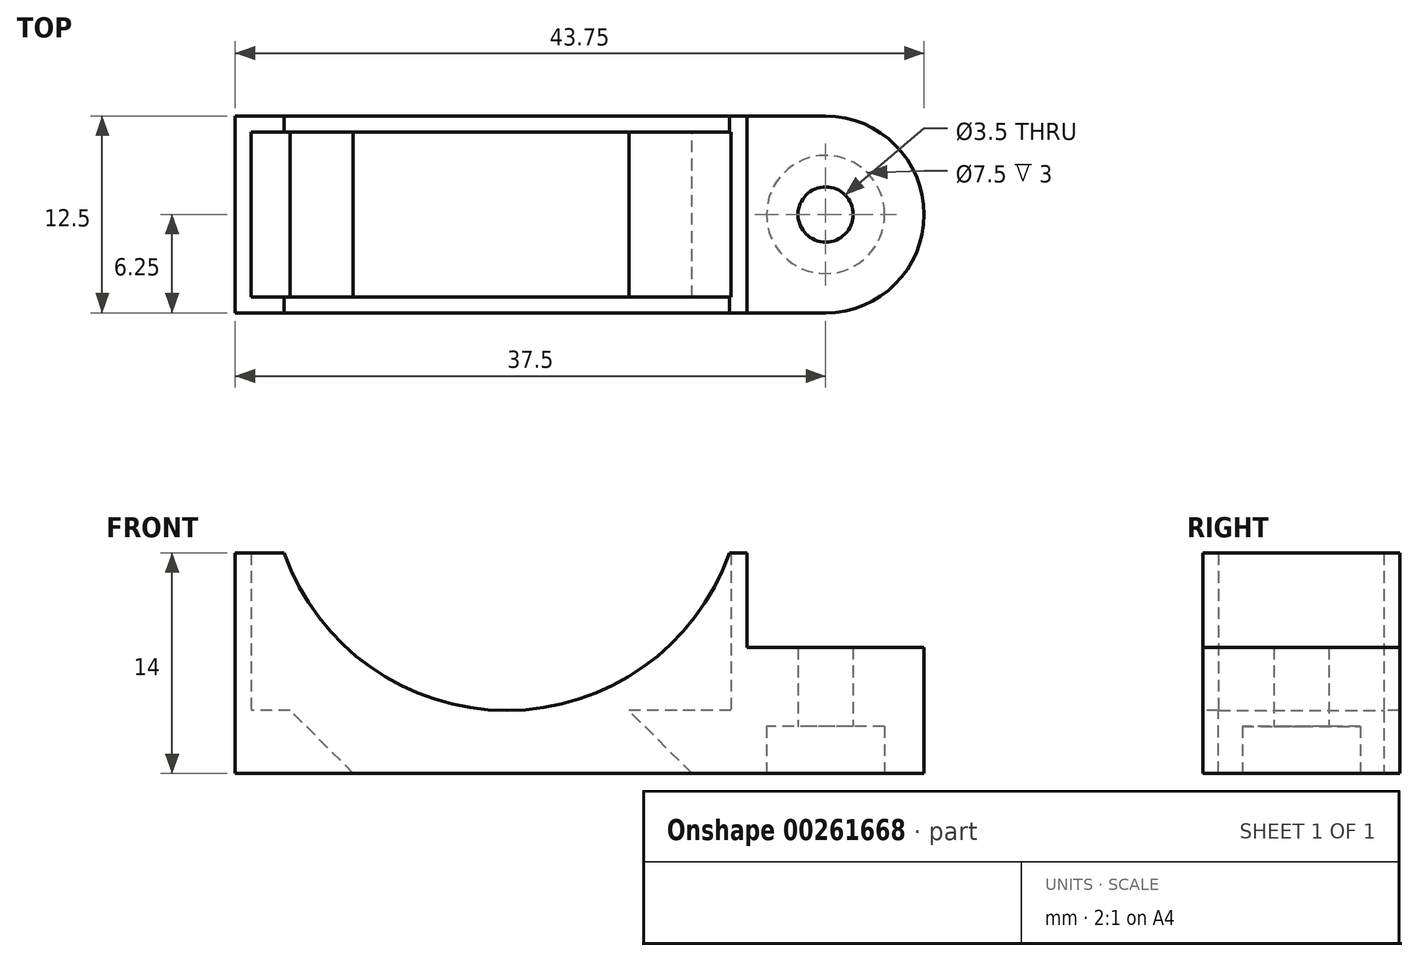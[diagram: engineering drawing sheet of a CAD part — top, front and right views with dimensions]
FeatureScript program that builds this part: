
annotation { "Feature Type Name" : "Feature", "Feature Type Description" : "" }
export const myFeature = defineFeature(function(context is Context, id is Id, definition is map)
    precondition{}
    {
        {
            var Q0;
            Q0=qCreatedBy(makeId("Top.planeOp"),FACE);
            var sketch = newSketch(context, id + "F0", { "sketchPlane" : qUnion([Q0])});
            skLineSegment(sketch, "E0.bottom", {"start": v(15.25, -5.25) * mm, "end": v(-15.25, -5.25) * mm});
            skLineSegment(sketch, "E0.top", {"start": v(15.25, 5.25) * mm, "end": v(-15.25, 5.25) * mm});
            skLineSegment(sketch, "E0.left", {"start": v(15.25, -5.25) * mm, "end": v(15.25, 5.25) * mm});
            skLineSegment(sketch, "E0.right", {"start": v(-15.25, -5.25) * mm, "end": v(-15.25, 5.25) * mm});
            skPoint(sketch, "E0.middle", {"position": v(0, 0) * mm});
            skLineSegment(sketch, "E1.0", {"start": v(-16.25, -6.25) * mm, "end": v(-16.25, 6.25) * mm});
            skLineSegment(sketch, "E1.1", {"start": v(16.25, -6.25) * mm, "end": v(-16.25, -6.25) * mm});
            skLineSegment(sketch, "E1.2", {"start": v(16.25, -6.25) * mm, "end": v(16.25, 6.25) * mm});
            skLineSegment(sketch, "E1.3", {"start": v(16.25, 6.25) * mm, "end": v(-16.25, 6.25) * mm});
            skArc(sketch, "E2", {"start": v(21.25, -6.25) * mm, "mid": v(27.5, 0) * mm, "end": v(21.25, 6.25) * mm});
            skLineSegment(sketch, "E3", {"start": v(16.25, -6.25) * mm, "end": v(21.25, -6.25) * mm});
            skLineSegment(sketch, "E4", {"start": v(16.25, 6.25) * mm, "end": v(21.25, 6.25) * mm});
            skLineSegment(sketch, "E5", {"start": v(8.75, 5.25) * mm, "end": v(8.75, -5.25) * mm});
            skCircle(sketch, "E6", {"center": v(21.25, 0) * mm, "radius": 1.75 * mm});
            skLineSegment(sketch, "E7", {"start": v(-8.75, -5.25) * mm, "end": v(-8.75, 5.25) * mm});
            skSolve(sketch);
        }
        {
            var Q0;
            Q0=makeQuery(id+"F0.imprint","IMPRINT",FACE,{"disambiguationData":[TD([[makeQuery(id+"F0.imprint","IMPRINT",EDGE,{"derivedFrom":sQuery(id+"F0.wireOp",EDGE,"E1.2")}),-1.0]])]});
            extrude(context, id + "F1", {"entities" : qUnion([Q0]), "depth" : 8 * mm});
        }
        {
            var Q0;
            {var subQ1=sQuery(id+"F0.wireOp",EDGE,"E0.left");Q0=makeQuery(id+"F0.imprint","IMPRINT",FACE,{"disambiguationData":[TD([[makeQuery(id+"F0.imprint","IMPRINT",EDGE,{"derivedFrom":subQ1}),-1.0]])]});}
            extrude(context, id + "F2", {"entities" : qUnion([Q0]), "operationType" : NewBodyOperationType.ADD, "depth" : 14 * mm});
        }
        {
            var Q0;
            {var subQ0=sQuery(id+"F0.wireOp",EDGE,"E0.left");Q0=makeQuery(id+"F0.imprint","IMPRINT",FACE,{"disambiguationData":[TD([[makeQuery(id+"F0.imprint","IMPRINT",EDGE,{"derivedFrom":subQ0}),1.0]])]});}
            var Q1;
            {var subQ0=sQuery(id+"F0.wireOp",EDGE,"E0.right");Q1=makeQuery(id+"F0.imprint","IMPRINT",FACE,{"disambiguationData":[TD([[makeQuery(id+"F0.imprint","IMPRINT",EDGE,{"derivedFrom":subQ0}),-1.0]])]});}
            extrude(context, id + "F3", {"entities" : qUnion([Q0, Q1]), "operationType" : NewBodyOperationType.ADD, "depth" : 4 * mm});
        }
        {
            var Q0;
            Q0=makeQuery(id+"F3.opExtrude","CAP_EDGE",EDGE,{"disambiguationData":[OSD([sQuery(id+"F0.wireOp",EDGE,"E7")])],"isStart":false});
            var Q1;
            Q1=makeQuery(id+"F3.opExtrude","CAP_EDGE",EDGE,{"disambiguationData":[OSD([sQuery(id+"F0.wireOp",EDGE,"E5")])],"isStart":true});
            chamfer(context, id + "F4", {"entities" : qUnion([Q0, Q1]), "width" : 4 * mm, "tangentPropagation" : true});
        }
        {
            var Q0;
            Q0=makeQuery(id+"F1.opExtrude","SWEPT_FACE",FACE,{"disambiguationData":[OSD([sQuery(id+"F0.wireOp",EDGE,"E1.1"),sQuery(id+"F0.wireOp",EDGE,"E3")])]});
            var sketch = newSketch(context, id + "F5", { "sketchPlane" : qUnion([Q0])});
            skCircle(sketch, "E8", {"center": v(1, 19) * mm, "radius": 15 * mm});
            skPoint(sketch, "E9", {"position": v(0, 19) * mm});
            skPoint(sketch, "E9.positionSnap0", {"position": v(0, 14) * mm});
            skSolve(sketch);
        }
        {
            var Q0;
            {var subQ0=sQuery(id+"F5.wireOp",EDGE,"E8");var subQ1=makeQuery(id+"F2.opExtrude","CAP_EDGE",EDGE,{"disambiguationData":[OSD([sQuery(id+"F0.wireOp",EDGE,"E1.1")])],"isStart":false});var subQ2=makeQuery(id+"F5.imprint","INTERSECT",VERTEX,{"disambiguationData":[OD(0.0)],"derivedFrom":[subQ1,subQ0]});Q0=makeQuery(id+"F5.imprint","IMPRINT",FACE,{"disambiguationData":[TD([[makeQuery(id+"F5.imprint","IMPRINT",EDGE,{"disambiguationData":[TD([[subQ2,-1.0]])],"derivedFrom":subQ0}),1.0]])]});}
            extrude(context, id + "F6", {"entities" : qUnion([Q0]), "operationType" : NewBodyOperationType.REMOVE, "oppositeDirection" : true, "depth" : 25 * mm});
        }
        {
            var Q0;
            Q0=makeQuery(id+"F0.imprint","IMPRINT",FACE,{"disambiguationData":[TD([[makeQuery(id+"F0.imprint","IMPRINT",EDGE,{"derivedFrom":sQuery(id+"F0.wireOp",EDGE,"E1.2")}),-1.0]])]});
            var sketch = newSketch(context, id + "F7", { "sketchPlane" : qUnion([Q0])});
            skCircle(sketch, "E10", {"center": v(21.25, 0) * mm, "radius": 3.75 * mm});
            skSolve(sketch);
        }
        {
            var Q0;
            Q0=makeQuery(id+"F7.imprint","IMPRINT",FACE,{"disambiguationData":[TD([[makeQuery(id+"F7.imprint","IMPRINT",EDGE,{"derivedFrom":sQuery(id+"F7.wireOp",EDGE,"E10")}),1.0]])]});
            extrude(context, id + "F8", {"entities" : qUnion([Q0]), "operationType" : NewBodyOperationType.REMOVE, "depth" : 3 * mm});
        }
    });
